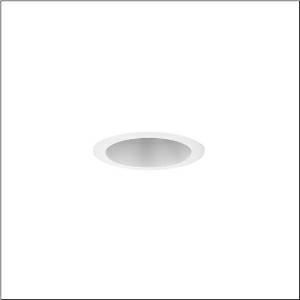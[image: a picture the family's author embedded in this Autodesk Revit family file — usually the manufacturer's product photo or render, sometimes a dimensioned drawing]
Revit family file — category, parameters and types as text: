
# Revit family: lunis_31-l_51dn15me31b
name_source: partatom
category: Lighting Fixtures
units: mm (PartAtom-declared; Revit-internal decimal feet)

## family parameters
Cut with Voids When Loaded = No
Host = Face
Light Source = No
Part Type = Normal
Room Calculation Point = No
Round Connector Dimension = Use Diameter
Shared = No

## types (1)
- --- (1 x LED, 1600 lm, 12 W, 3000K)
    Apparent Load = 12 VA
    CIE Flux Codes = 93 98 100 100 100
    Color Rendering = 80
    Color Temperature = 3000K
    Default Elevation = 1800 mm
    Description = Lunis 31, -L, downlight, light control with reflector, light emission: direct distribution, LED rated luminous flux: 1.600lm, light colour: 830, mains connection: 220..240V, AC, 50/60Hz, housing, of aluminium, white, protection rating (complete): IP20, protection rating (on room side): IP54, insulation class (complete): insulation class II (safety insulation), certification: CE, packaging unit: 1 piece
    Height = 0 mm  [stored 0 ft]
    Lamp = 1 x LED
    Lamp Light Flux = 1600 lm
    Lamp Power = 12 W
    Lamp count = 1
    Length = 188 mm  [stored 0.616798 ft]
    Luminous efficacy = 133 lm/W
    Manufacturer = Siteco
    ModVariant = No
    Model = 51DN15ME31B
    Mounting Place = Ceiling
    Mounting Type = Recessed
    Number of Poles = 1
    OnlyDefault = Yes
    Power Factor = 1
    Product Name = Lunis 31-L
    Product group = downlight
    ProductGroupID = 400
    Protection Class = Protection class II
    Protection Degree = IP 20
    RLX_Detail_Level = 1
    RLX_Emergency_Light_Flux = 0 lm
    RLX_Emergency_Type = 0
    RLX_Emergency_Type_DB = No
    RlxData = <blob elided: 22193 chars, md5=a11a6061>
    Socket = socket
    Standby Power = 0 W
    System Light Flux = 1600 lm
    System Power = 12 W
    Type Comments = individual setting: luminous flux: 100 % | (OFF | ON) | 300 mA
    Type Image = l_1345911.jpg
    URL = http://relux.com
    VarID = @adj_010143
    Voltage = 0 V
    Weight = 0.00 kg
    Width = 0 mm  [stored 0 ft]

note: [stored X ft] marks values corroborated as IEEE doubles in the binary element streams (Revit-internal decimal feet)

## geometry (parser evidence)
native form markers: Blend x4, Sweep x11
no freeform markers — native parametric forms only
